# Revit family: PRD_FrankeWS_JntrlUnits_SiriusCleanersSink_WB500GV
name_source: partatom
category: Plumbing Fixtures
revit_build: Autodesk Revit 2018 (Build: 20190510_1515(x64)
units: mm (PartAtom-declared; Revit-internal decimal feet)

## family parameters
Cut with Voids When Loaded = No
Host = Face
OmniClass Number = 23.45.05.14.14
OmniClass Title = Sinks/Lavatories
Part Type = Normal
Room Calculation Point = No
Round Connector Dimension = Use Diameter
Shared = No

## types (1)
- WB500GV
    AssetType = Fixed
    BIMObjectName = PRD_AR_JanitorialUnits_SiriusCleanersSink_WB500GV
    Category = Pr_40_20_96_44, Janitorial sinks
    Color = Stainless steel
    Default Elevation = 850 mm  [stored 2.78871 ft]
    Description = General purpose sink for wall mounting, stainless steel, surface satin finished, material thickness 1.5 mm, seamless welded bowl with dimensions 370x340x160 mm, rounded edges, 1 1/2 plug waste with plastic overflow pipe, drainage back left, 30 mm rear upstand, incl. stainless steel grid with rubber bumps, incl. stainless steel screws and dowels.
    DrainSize = DN 40 (1 1/2 inch.)
    DurationUnit = year
    Features = stainless steel, 1.5 mm, satin finished, wall mounting, 500x180x500 mm (WxHxD)
    Finish = Satin finished
    FinishAndMaterial = Stainless steel 1.4301
    Form = Stainless steel cleaners sink
    GrossWeight = 6.50 kg
    IfcExportAs = IfcSanitaryTerminalType
    IfcExportType = SINK
    IntegralAccessories = incl. stainless steel grid with rubber bumps, incl. stainless steel screws and dowels
    Manufacturer = KWC Group AG
    ManufacturerName = KWC Group AG
    ManufacturerURL = www.kwc.com
    Material = Stainless steel
    Model = WB500GV
    ModelNumber = 2000057408
    ModelReference = WB500GV
    NBSDescription = Janitorial units
    NBSReference = 45-35-70/401
    Name = Sirius cleaners sink WB500GV
    NetWeight = 5.30 kg
    NominalDepth = 500 mm  [stored 1.64042 ft]
    NominalLength = 180 mm  [stored 0.590551 ft]
    NominalWidth = 500 mm  [stored 1.64042 ft]
    ProductInformation = https://pim.kwc.com
    Shape = Rectangular
    SinkMaterial = PRD_AR_StainlessSteel_SatinFinished
    SinkMounting = WallHung
    SinkType = Other
    Size = 500 x 500 x 180 mm
    URL = www.kwc.com
    Uniclass2015Code = Pr_40_20_96_44
    Uniclass2015Title = Janitorial sinks
    Uniclass2015Version = Products v1.10
    Version = 1
    WarrantyDurationUnit = year
    WasteSize = 40  [stored 0.131234 ft]
    WaterSupplyOverflowAndWasteHolesOverflow = Stand pipe overflow
    WaterSupplyOverflowAndWasteHolesWaste = Left-Back-Corner
    WaterSupplyOverflowAndWasteHolesWaterSupply = No tapholes

note: [stored X ft] marks values corroborated as IEEE doubles in the binary element streams (Revit-internal decimal feet)

## geometry (parser evidence)
native form markers: Sweep x6
no freeform markers — native parametric forms only
